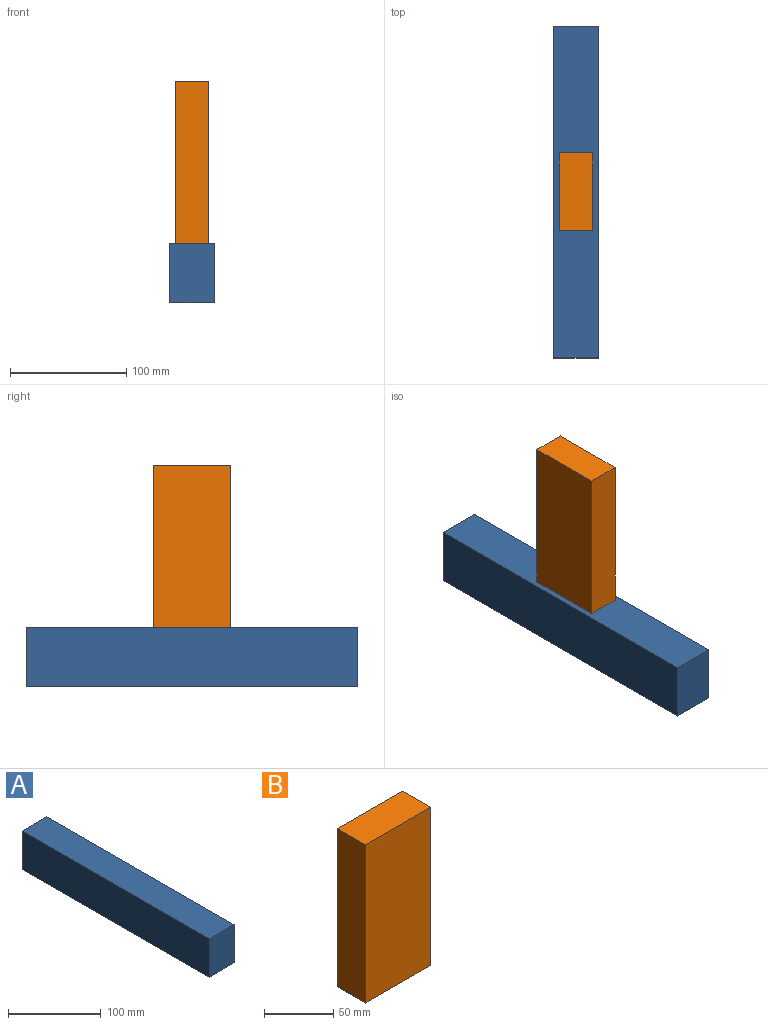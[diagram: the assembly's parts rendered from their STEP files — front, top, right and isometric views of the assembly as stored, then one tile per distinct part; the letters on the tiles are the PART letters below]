
ASSEMBLY  parts=2 mates=2
PART A: 6 faces, bbox 38.1x285.8x50.8 mm
  f0: plane 285.75x38.1mm, normal (0,0,1), area 10887.1mm2, adj f1,f3,f4,f5
  f1: plane 285.75x50.8mm, normal (-1,0,0), area 14516.1mm2, adj f0,f2,f4,f5
  f2: plane 285.75x38.1mm, normal (0,0,-1), area 10887.1mm2, adj f1,f3,f4,f5
  f3: plane 285.75x50.8mm, normal (1,0,0), area 14516.1mm2, adj f0,f2,f4,f5
  f4: plane 50.8x38.1mm, normal (0,-1,0), area 1935.5mm2, adj f0,f1,f2,f3
  f5: plane 50.8x38.1mm, normal (0,1,0), area 1935.5mm2, adj f0,f1,f2,f3
PART B: 6 faces, bbox 66.7x28.6x139.7 mm
  f0: plane 139.7x66.68mm, normal (0,1,0), area 9314.5mm2, adj f1,f3,f4,f5
  f1: plane 139.7x28.58mm, normal (-1,0,0), area 3991.9mm2, adj f0,f2,f4,f5
  f2: plane 139.7x66.68mm, normal (0,-1,0), area 9314.5mm2, adj f1,f3,f4,f5
  f3: plane 139.7x28.58mm, normal (1,0,0), area 3991.9mm2, adj f0,f2,f4,f5
  f4: plane 66.68x28.58mm, normal (0,0,1), area 1905.2mm2, adj f0,f1,f2,f3
  f5: plane 66.68x28.58mm, normal (0,0,-1), area 1905.2mm2, adj f0,f1,f2,f3
PLACE A t=(0,0,-25.4)mm
PLACE B rot(axis=(0,0,1),90deg) t=(0,0,69.85)mm
MATE fastened B.f5 <-> A.f0  axis (0,0,-1) through (0,0,0)mm
MATE slider B.f5 <-> A.f0  axis (0,0,-1) through (0,0,0)mm
